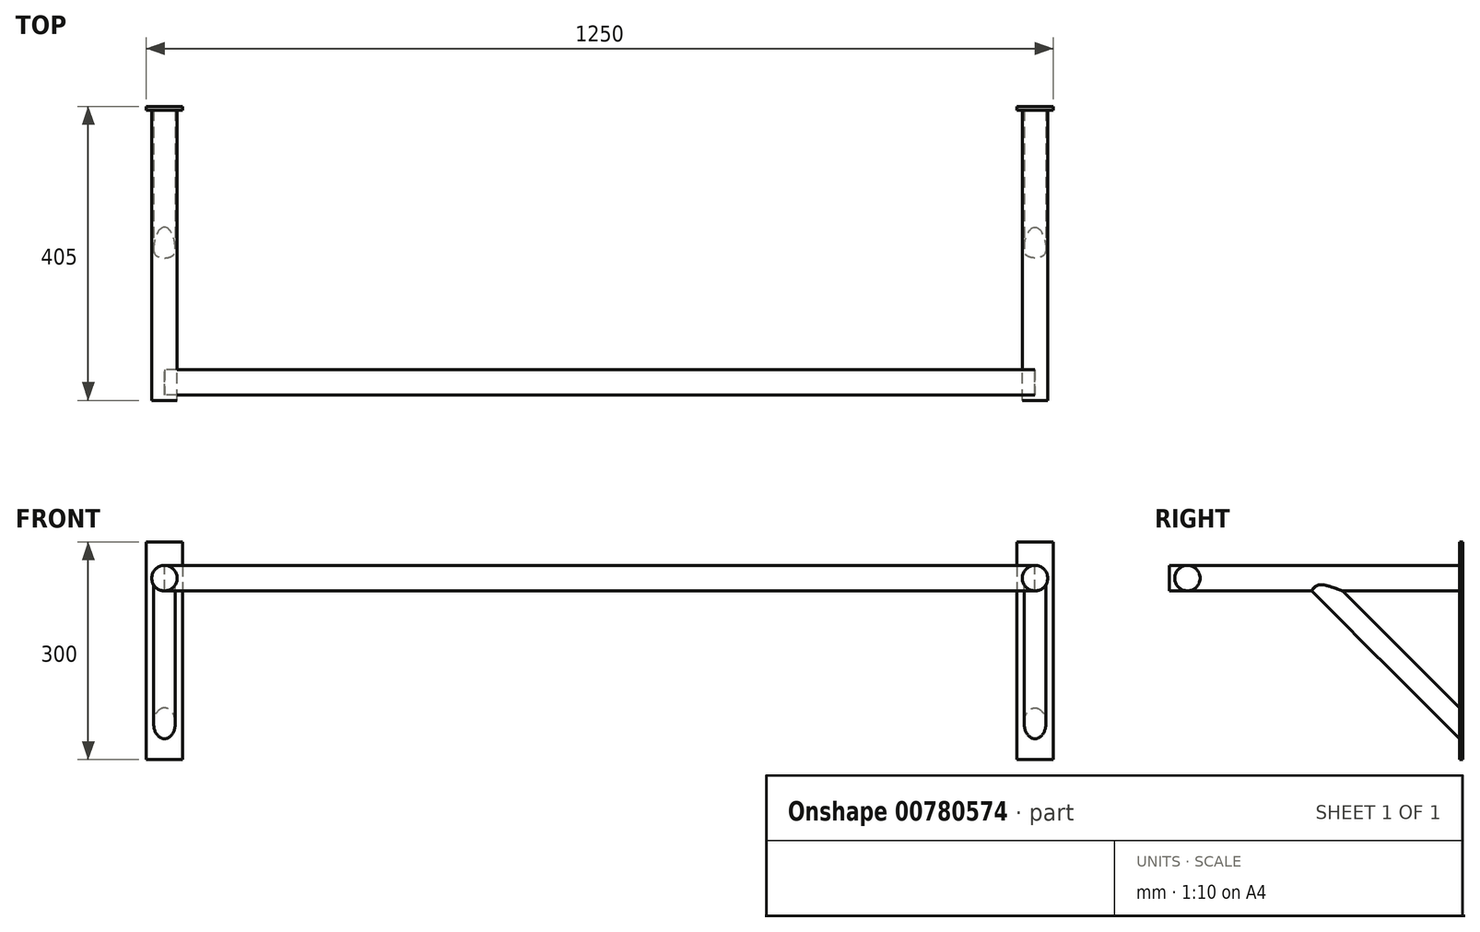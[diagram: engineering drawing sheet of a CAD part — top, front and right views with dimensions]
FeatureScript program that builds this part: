
annotation { "Feature Type Name" : "Feature", "Feature Type Description" : "" }
export const myFeature = defineFeature(function(context is Context, id is Id, definition is map)
    precondition{}
    {
        {
            var Q0;
            Q0=qCreatedBy(makeId("Front.planeOp"),FACE);
            var sketch = newSketch(context, id + "F0", { "sketchPlane" : qUnion([Q0])});
            skLineSegment(sketch, "E0.bottom", {"start": v(-625, 50) * mm, "end": v(-575, 50) * mm});
            skLineSegment(sketch, "E0.top", {"start": v(-625, -250) * mm, "end": v(-575, -250) * mm});
            skLineSegment(sketch, "E0.left", {"start": v(-625, 50) * mm, "end": v(-625, -250) * mm});
            skLineSegment(sketch, "E0.right", {"start": v(-575, 50) * mm, "end": v(-575, -250) * mm});
            skSolve(sketch);
        }
        {
            var Q0;
            Q0=makeQuery(id+"F0.imprint","IMPRINT",FACE,{"disambiguationData":[TD([[makeQuery(id+"F0.imprint","IMPRINT",EDGE,{"derivedFrom":sQuery(id+"F0.wireOp",EDGE,"E0.bottom")}),-1.0]])]});
            extrude(context, id + "F1", {"entities" : qUnion([Q0]), "depth" : 5 * mm, "offsetDistance" : 25 * mm});
        }
        {
            var Q0;
            Q0=makeQuery(id+"F1.opExtrude","CAP_FACE",FACE,{"disambiguationData":[OSD([sQuery(id+"F0.wireOp",EDGE,"E0.bottom"),sQuery(id+"F0.wireOp",EDGE,"E0.top"),sQuery(id+"F0.wireOp",EDGE,"E0.left"),sQuery(id+"F0.wireOp",EDGE,"E0.right")])],"isStart":false});
            var sketch = newSketch(context, id + "F2", { "sketchPlane" : qUnion([Q0])});
            skCircle(sketch, "E1", {"center": v(-600, 0) * mm, "radius": 17.5 * mm});
            skSolve(sketch);
        }
        {
            var Q0;
            Q0=makeQuery(id+"F2.imprint","IMPRINT",FACE,{"disambiguationData":[TD([[makeQuery(id+"F2.imprint","IMPRINT",EDGE,{"derivedFrom":sQuery(id+"F2.wireOp",EDGE,"E1")}),1.0]])]});
            extrude(context, id + "F3", {"entities" : qUnion([Q0]), "operationType" : NewBodyOperationType.ADD, "depth" : 400 * mm, "offsetDistance" : 25 * mm});
        }
        {
            var Q0;
            Q0=qCreatedBy(makeId("Right.planeOp"),FACE);
            cPlane(context, id + "F4", {"entities" : qUnion([Q0]), "cplaneType" : CPlaneType.OFFSET, "offset" : 600 * mm, "oppositeDirection" : true, "width" : 150 * mm, "height" : 150 * mm});
        }
        {
            var Q0;
            Q0=qCreatedBy(id+"F4.planeOp",FACE);
            var sketch = newSketch(context, id + "F5", { "sketchPlane" : qUnion([Q0])});
            skLineSegment(sketch, "E2", {"start": v(-5, -200) * mm, "end": v(-205, 0) * mm});
            skSolve(sketch);
        }
        {
            var Q0;
            Q0=sQuery(id+"F5.wireOp",VERTEX,"E2.end");
            var Q1;
            Q1=sQuery(id+"F5.wireOp",EDGE,"E2");
            cPlane(context, id + "F6", {"entities" : qUnion([Q0, Q1]), "cplaneType" : CPlaneType.LINE_POINT, "offset" : 25 * mm, "width" : 150 * mm, "height" : 150 * mm});
        }
        {
            var Q0;
            Q0=qCreatedBy(id+"F6.planeOp",FACE);
            var sketch = newSketch(context, id + "F7", { "sketchPlane" : qUnion([Q0])});
            skCircle(sketch, "E3", {"center": v(-600, -144.96) * mm, "radius": 15 * mm});
            skSolve(sketch);
        }
        {
            var Q0;
            Q0 = qSketchRegion(id + "F7", true);
            var Q1;
            Q1=makeQuery(id+"F1.opExtrude","CAP_FACE",FACE,{"disambiguationData":[OSD([sQuery(id+"F0.wireOp",EDGE,"E0.bottom"),sQuery(id+"F0.wireOp",EDGE,"E0.top"),sQuery(id+"F0.wireOp",EDGE,"E0.left"),sQuery(id+"F0.wireOp",EDGE,"E0.right")])],"isStart":false});
            extrude(context, id + "F8", {"entities" : qUnion([Q0]), "operationType" : NewBodyOperationType.ADD, "endBound" : BoundingType.UP_TO_SURFACE, "oppositeDirection" : true, "depth" : 25 * mm, "endBoundEntityFace" : qUnion([Q1]), "offsetDistance" : 25 * mm});
        }
        {
            var Q0;
            Q0=makeQuery(id+"F1.opExtrude","SWEPT_BODY",BODY,{"disambiguationData":[OSD([sQuery(id+"F0.wireOp",EDGE,"E0.bottom"),sQuery(id+"F0.wireOp",EDGE,"E0.top"),sQuery(id+"F0.wireOp",EDGE,"E0.left"),sQuery(id+"F0.wireOp",EDGE,"E0.right")])]});
            var Q1;
            Q1=qCreatedBy(makeId("Right.planeOp"),FACE);
            mirror(context, id + "F9", {"entities" : qUnion([Q0]), "mirrorPlane" : qUnion([Q1])});
        }
        {
            var Q0;
            Q0=qCreatedBy(makeId("Right.planeOp"),FACE);
            var sketch = newSketch(context, id + "F10", { "sketchPlane" : qUnion([Q0])});
            skCircle(sketch, "E4", {"center": v(-380, 0) * mm, "radius": 17.5 * mm});
            skSolve(sketch);
        }
        {
            var Q0;
            Q0=makeQuery(id+"F10.imprint","IMPRINT",FACE,{"disambiguationData":[TD([[makeQuery(id+"F10.imprint","IMPRINT",EDGE,{"derivedFrom":sQuery(id+"F10.wireOp",EDGE,"E4")}),1.0]])]});
            extrude(context, id + "F11", {"entities" : qUnion([Q0]), "endBound" : BoundingType.SYMMETRIC, "depth" : 1200 * mm, "offsetDistance" : 25 * mm});
        }
    });
